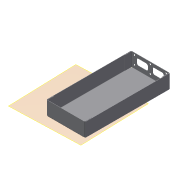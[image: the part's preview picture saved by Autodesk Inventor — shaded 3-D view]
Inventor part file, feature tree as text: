
AUTODESK INVENTOR PART (.ipt)
format: ipt  version: 2015 (Build 190159000, 159)  size: 294,912 bytes
history: native  units: mm
features: reference x24, sheet_metal_op x7, other x6, sketch x5, plane x1, projected_geometry x1
ambient origin geometry x8: Origin, YZ Plane, XZ Plane, XY Plane, X Axis, Y Axis, Z Axis, Center Point
bodies: Solid1 (feature_tree)
feature tree (44):
  plane  "Work Plane1"
  sheet_metal_op  "Face1"
  sheet_metal_op  "Flange1"
  sheet_metal_op  "Flange2"
  other  "A-Side Definition"
  sketch  "Sketch4"  dims[d4=0.9mm]
  sketch  "Sketch1"  dims[d0=240.0mm]
  other  "Plate1"
  sketch  "Sketch2"  dims[d1=110.0mm]
  other  "Plate2"
  sheet_metal_op  "Bend1"
  sheet_metal_op  "Corner1"
  sketch  "Sketch3"  dims[d3=0.9mm]
  other  "Plate3"
  sheet_metal_op  "Bend2"
  sheet_metal_op  "Corner2"
  sketch  "Sketch5"  dims[d5=0.45mm d6=1.8mm d7=0.9mm d8=40.0mm d9=90.0deg d10=0.9mm d11=3.6mm d12=0.9mm d13=0.9mm d14=0.9mm d15=0.45mm d16=1.8mm d17=0.9mm d18=20.0mm d19=90.0deg d20=0.9mm d21=3.6mm d22=0.9mm d23=0.9mm d25=1.0mm d26=1.0mm d27=0.9mm d28=0.0mm]
  projected_geometry  "Projected Loop1"
  reference  "Reference1"
  reference  "Reference2"
  reference  "Reference3"
  reference  "Reference4"
  reference  "Reference5"
  reference  "Reference6"
  reference  "Reference7"
  reference  "Reference8"
  reference  "Reference9"
  reference  "Reference10"
  reference  "Reference11"
  reference  "Reference12"
  reference  "Reference13"
  reference  "Reference14"
  reference  "Reference15"
  reference  "Reference16"
  reference  "Reference17"
  reference  "Reference18"
  reference  "Reference19"
  reference  "Reference20"
  reference  "Reference21"
  reference  "Reference22"
  reference  "Reference23"
  reference  "Reference24"
  other  "Cut1"
  other  "Definition1"
